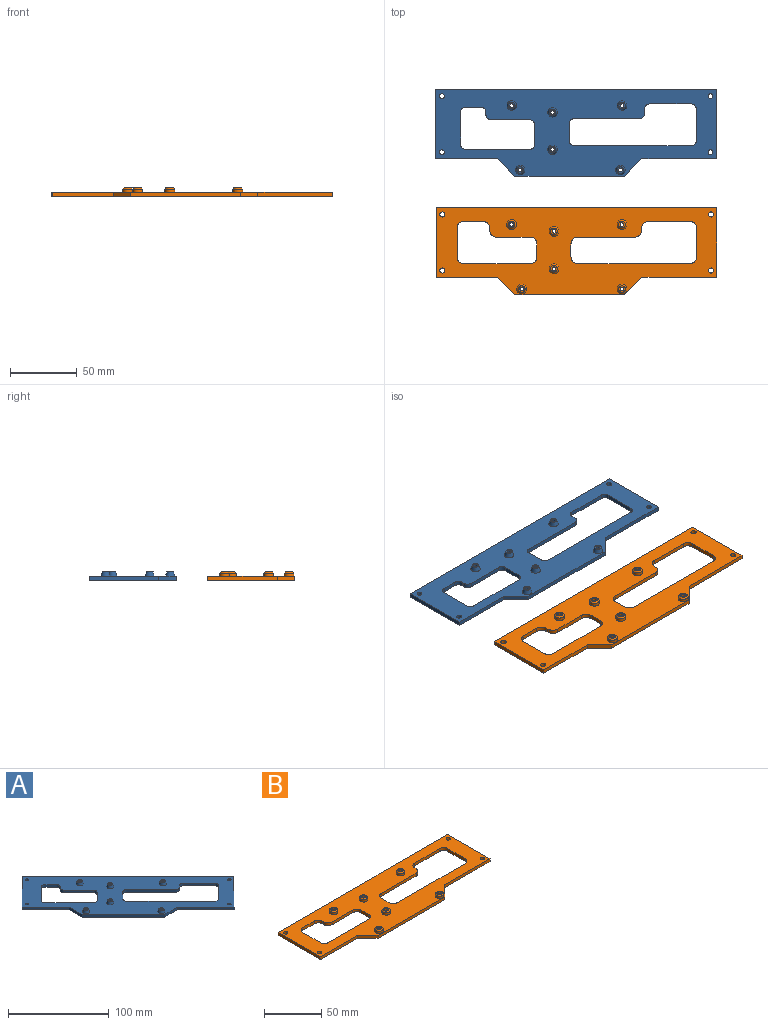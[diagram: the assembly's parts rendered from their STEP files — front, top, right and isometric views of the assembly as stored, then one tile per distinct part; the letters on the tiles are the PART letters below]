
ASSEMBLY  parts=2 mates=2
PART A: 56 faces, bbox 185.7x185.6x6.5 mm
  f0: plane 185.65x185.62mm, normal (0,0,-1), area 8330.5mm2, adj f2,f3,f4,f5,f6,f7,f8,f9
  f1: plane 185.65x185.62mm, normal (0,0,1), area 8139.6mm2, adj f2,f3,f4,f5,f6,f7,f8,f14
  f2: plane 148.96x148.96mm, normal (0.71,0.71,0), area 642.1mm2, adj f0,f1,f3,f18
  f3: plane 36.69x36.69mm, normal (-0.71,0.71,0), area 158.2mm2, adj f0,f1,f2,f4
  f4: plane 33.09x33.09mm, normal (-0.71,-0.71,0), area 142.6mm2, adj f0,f1,f3,f5
  f5: plane 18.17x3.05mm, normal (-1,0,0), area 55.4mm2, adj f0,f1,f4,f6
  f6: plane 58.05x58.05mm, normal (-0.71,-0.71,0), area 250.2mm2, adj f0,f1,f5,f7
  f7: plane 18.24x3.05mm, normal (0,-1,0), area 55.6mm2, adj f0,f1,f6,f8
  f8: plane 39.62x39.62mm, normal (-0.71,-0.71,0), area 170.8mm2, adj f0,f1,f7,f18
  f9: cylinder r=1.4mm len=6.48mm, axis (0,0,1), area 57mm2, adj f0,f21
  f10: cylinder r=1.4mm len=6.48mm, axis (0,0,1), area 57mm2, adj f0,f23
  f11: cylinder r=1.4mm len=6.48mm, axis (0,0,1), area 57mm2, adj f0,f20
  f12: cylinder r=1.4mm len=6.48mm, axis (0,0,1), area 57mm2, adj f0,f24
  f13: cylinder r=1.4mm len=6.48mm, axis (0,0,1), area 57mm2, adj f0,f25
  f14: cylinder r=1.8mm len=3.6mm, axis (0,0,1), area 34.5mm2, adj f0,f1
  f15: cylinder r=1.8mm len=3.6mm, axis (0,0,1), area 34.5mm2, adj f0,f1
  f16: cylinder r=1.8mm len=3.6mm, axis (0,0,1), area 34.5mm2, adj f0,f1
  f17: cylinder r=1.8mm len=3.6mm, axis (0,0,1), area 34.5mm2, adj f0,f1
  f18: plane 36.66x36.66mm, normal (0.71,-0.71,0), area 158mm2, adj f0,f1,f2,f8
  f19: cylinder r=1.4mm len=6.48mm, axis (0,0,1), area 57mm2, adj f0,f22
  f20: plane 4.88x4.88mm, normal (0,0,1), area 12.5mm2, adj f11,f29
  f21: plane 4.91x4.91mm, normal (0,0,1), area 12.8mm2, adj f9,f28
  f22: plane 4.91x4.91mm, normal (0,0,1), area 12.8mm2, adj f19,f26
  f23: plane 4.9x4.9mm, normal (0,0,1), area 12.7mm2, adj f10,f27
  f24: plane 4.89x4.89mm, normal (0,0,1), area 12.6mm2, adj f12,f30
  f25: plane 4.88x4.88mm, normal (0,0,1), area 12.5mm2, adj f13,f31
  f26: cone r=2.46mm half-angle=16.7deg, axis (0,0,-1), area 66.8mm2, adj f1,f22
  f27: cone r=2.45mm half-angle=16.7deg, axis (0,0,-1), area 66.7mm2, adj f1,f23
  f28: cone r=2.45mm half-angle=16.7deg, axis (0,0,-1), area 66.8mm2, adj f1,f21
  f29: cone r=2.44mm half-angle=16.7deg, axis (0,0,-1), area 66.4mm2, adj f1,f20
  f30: cone r=2.44mm half-angle=16.7deg, axis (0,0,-1), area 66.6mm2, adj f1,f24
  f31: cone r=2.44mm half-angle=16.7deg, axis (0,0,-1), area 66.4mm2, adj f1,f25
  f32: plane 61.76x61.76mm, normal (0.71,0.71,0), area 266.2mm2, adj f0,f1,f33,f43
  f33: cylinder r=3.81mm len=5.39mm, axis (0,0,1), area 18.2mm2, adj f0,f1,f32,f34
  f34: plane 16.81x16.81mm, normal (-0.71,0.71,0), area 72.5mm2, adj f0,f1,f33,f35
  f35: cylinder r=3.81mm len=5.39mm, axis (0,0,1), area 18.2mm2, adj f0,f1,f34,f36
  f36: plane 21.92x21.92mm, normal (-0.71,-0.71,0), area 94.5mm2, adj f0,f1,f35,f37
  f37: cylinder r=3.81mm len=5.39mm, axis (0,0,1), area 18.2mm2, adj f0,f1,f36,f38
  f38: plane 3.05x2.38mm, normal (0.71,-0.71,0), area 10.3mm2, adj f0,f1,f37,f39
  f39: cylinder r=3.81mm len=5.39mm, axis (0,0,1), area 18.2mm2, adj f0,f1,f38,f40
  f40: plane 34.45x34.45mm, normal (-0.71,-0.71,0), area 148.5mm2, adj f0,f1,f39,f41
  f41: cylinder r=3.81mm len=5.39mm, axis (0,0,1), area 18.2mm2, adj f0,f1,f40,f42
  f42: plane 9.04x9.04mm, normal (0.71,-0.71,0), area 39mm2, adj f0,f1,f41,f43
  f43: cylinder r=3.81mm len=5.39mm, axis (0,0,1), area 18.2mm2, adj f0,f1,f32,f42
  f44: plane 10.17x10.17mm, normal (-0.71,0.71,0), area 43.8mm2, adj f0,f1,f45,f55
  f45: cylinder r=3.81mm len=5.39mm, axis (0,0,1), area 18.2mm2, adj f0,f1,f44,f46
  f46: plane 20.48x20.48mm, normal (-0.71,-0.71,0), area 88.3mm2, adj f0,f1,f45,f47
  f47: cylinder r=3.81mm len=5.39mm, axis (0,0,1), area 18.2mm2, adj f0,f1,f46,f48
  f48: plane 3.05x1.34mm, normal (-0.71,0.71,0), area 5.8mm2, adj f0,f1,f47,f49
  f49: cylinder r=3.81mm len=5.39mm, axis (0,0,1), area 18.2mm2, adj f0,f1,f48,f50
  f50: plane 8.05x8.05mm, normal (-0.71,-0.71,0), area 34.7mm2, adj f0,f1,f49,f51
  f51: cylinder r=3.81mm len=5.39mm, axis (0,0,1), area 18.2mm2, adj f0,f1,f50,f52
  f52: plane 16.9x16.9mm, normal (0.71,-0.71,0), area 72.8mm2, adj f0,f1,f51,f53
  f53: cylinder r=3.81mm len=5.39mm, axis (0,0,1), area 18.2mm2, adj f0,f1,f52,f54
  f54: plane 33.93x33.93mm, normal (0.71,0.71,0), area 146.2mm2, adj f0,f1,f53,f55
  f55: cylinder r=3.81mm len=5.39mm, axis (0,0,1), area 18.2mm2, adj f0,f1,f44,f54
PART B: 62 faces, bbox 209.6x64.9x6.5 mm
  f0: plane 209.55x64.92mm, normal (0,0,1), area 8053.7mm2, adj f2,f3,f4,f5,f6,f7,f8,f9
  f1: plane 209.55x64.92mm, normal (0,0,-1), area 8263.8mm2, adj f2,f3,f4,f5,f6,f7,f8,f9
  f2: plane 45.69x3mm, normal (0,-1,0), area 137.1mm2, adj f0,f1,f5,f11
  f3: plane 52.07x3mm, normal (1,0,0), area 156.2mm2, adj f0,f1,f4,f9
  f4: plane 209.55x3mm, normal (0,1,0), area 628.6mm2, adj f0,f1,f3,f5
  f5: plane 52.07x3mm, normal (-1,0,0), area 156.2mm2, adj f0,f1,f2,f4
  f6: cylinder r=1.91mm len=3.81mm, axis (0,0,-1), area 35.9mm2, adj f0,f1
  f7: cylinder r=1.91mm len=3.81mm, axis (0,0,-1), area 35.9mm2, adj f0,f1
  f8: cylinder r=1.91mm len=3.81mm, axis (0,0,-1), area 35.9mm2, adj f0,f1
  f9: plane 56.03x3mm, normal (0,-1,0), area 168.1mm2, adj f0,f1,f3,f13
  f10: cylinder r=1.91mm len=3.81mm, axis (0,0,-1), area 35.9mm2, adj f0,f1
  f11: plane 12.87x12.85mm, normal (-0.71,-0.71,0), area 54.6mm2, adj f0,f1,f2,f12
  f12: plane 82.09x3mm, normal (0,-1,0), area 246.3mm2, adj f0,f1,f11,f13
  f13: plane 12.87x12.85mm, normal (0.71,-0.71,0), area 54.6mm2, adj f0,f1,f9,f12
  f14: cylinder r=1.4mm len=6.51mm, axis (0,0,1), area 57.1mm2, adj f1,f31
  f15: cylinder r=1.4mm len=6.51mm, axis (0,0,1), area 57.1mm2, adj f1,f23
  f16: cylinder r=1.4mm len=6.51mm, axis (0,0,1), area 57.1mm2, adj f1,f29
  f17: cylinder r=1.4mm len=6.51mm, axis (0,0,1), area 57.1mm2, adj f1,f21
  f18: cylinder r=1.4mm len=6.51mm, axis (0,0,1), area 57.1mm2, adj f1,f27
  f19: cylinder r=1.4mm len=6.51mm, axis (0,0,1), area 57.1mm2, adj f1,f25
  f20: cylinder r=3.62mm len=7.24mm, axis (0,0,-1), area 53.7mm2, adj f0,f37
  f21: plane 4.95x4.95mm, normal (0,0,1), area 13.1mm2, adj f17,f37
  f22: cylinder r=3.62mm len=7.24mm, axis (0,0,-1), area 53.7mm2, adj f0,f36
  f23: plane 4.95x4.95mm, normal (0,0,1), area 13.1mm2, adj f15,f36
  f24: cylinder r=3.62mm len=7.24mm, axis (0,0,-1), area 53.7mm2, adj f0,f35
  f25: plane 4.95x4.95mm, normal (0,0,1), area 13.1mm2, adj f19,f35
  f26: cylinder r=3.62mm len=7.24mm, axis (0,0,-1), area 53.7mm2, adj f0,f34
  f27: plane 4.95x4.95mm, normal (0,0,1), area 13.1mm2, adj f18,f34
  f28: cylinder r=3.62mm len=7.24mm, axis (0,0,-1), area 53.7mm2, adj f0,f33
  f29: plane 4.95x4.95mm, normal (0,0,1), area 13.1mm2, adj f16,f33
  f30: cylinder r=3.62mm len=7.24mm, axis (0,0,-1), area 53.7mm2, adj f0,f32
  f31: plane 4.95x4.95mm, normal (0,0,1), area 13.1mm2, adj f14,f32
  f32: cone r=2.48mm half-angle=45deg, axis (0,0,-1), area 31mm2, adj f30,f31
  f33: cone r=2.48mm half-angle=45deg, axis (0,0,-1), area 31mm2, adj f28,f29
  f34: cone r=2.48mm half-angle=45deg, axis (0,0,-1), area 31mm2, adj f26,f27
  f35: cone r=2.48mm half-angle=45deg, axis (0,0,-1), area 31mm2, adj f24,f25
  f36: cone r=2.48mm half-angle=45deg, axis (0,0,-1), area 31mm2, adj f22,f23
  f37: cone r=2.48mm half-angle=45deg, axis (0,0,-1), area 31mm2, adj f20,f21
  f38: cylinder r=5.08mm len=5.08mm, axis (0,0,1), area 23.9mm2, adj f0,f1,f39,f49
  f39: plane 9.72x3mm, normal (-1,0,0), area 29.2mm2, adj f0,f1,f38,f40
  f40: cylinder r=5.08mm len=5.08mm, axis (0,0,1), area 23.9mm2, adj f0,f1,f39,f41
  f41: plane 25.28x3mm, normal (0,-1,0), area 75.8mm2, adj f0,f1,f40,f42
  f42: cylinder r=5.08mm len=5.08mm, axis (0,0,1), area 23.9mm2, adj f0,f1,f41,f43
  f43: plane 3x1.71mm, normal (-1,0,0), area 5.1mm2, adj f0,f1,f42,f44
  f44: cylinder r=5.08mm len=5.08mm, axis (0,0,1), area 23.9mm2, adj f0,f1,f43,f45
  f45: plane 14.21x3mm, normal (0,-1,0), area 42.6mm2, adj f0,f1,f44,f46
  f46: cylinder r=5.08mm len=5.08mm, axis (0,0,1), area 23.9mm2, adj f0,f1,f45,f47
  f47: plane 21.59x3mm, normal (1,0,0), area 64.8mm2, adj f0,f1,f46,f48
  f48: cylinder r=5.08mm len=5.08mm, axis (0,0,1), area 23.9mm2, adj f0,f1,f47,f49
  f49: plane 49.65x3mm, normal (0,1,0), area 148.9mm2, adj f0,f1,f38,f48
  f50: plane 9.72x3mm, normal (1,0,0), area 29.2mm2, adj f0,f1,f51,f61
  f51: cylinder r=5.08mm len=5.08mm, axis (0,0,1), area 23.9mm2, adj f0,f1,f50,f52
  f52: plane 83.7x3mm, normal (0,1,0), area 251.1mm2, adj f0,f1,f51,f53
  f53: cylinder r=5.08mm len=5.08mm, axis (0,0,1), area 23.9mm2, adj f0,f1,f52,f54
  f54: plane 21.59x3mm, normal (-1,0,0), area 64.8mm2, adj f0,f1,f53,f55
  f55: cylinder r=5.08mm len=5.08mm, axis (0,0,1), area 23.9mm2, adj f0,f1,f54,f56
  f56: plane 30.78x3mm, normal (0,-1,0), area 92.3mm2, adj f0,f1,f55,f57
  f57: cylinder r=5.08mm len=5.08mm, axis (0,0,1), area 23.9mm2, adj f0,f1,f56,f58
  f58: plane 3x1.71mm, normal (1,0,0), area 5.1mm2, adj f0,f1,f57,f59
  f59: cylinder r=5.08mm len=5.08mm, axis (0,0,1), area 23.9mm2, adj f0,f1,f58,f60
  f60: plane 42.77x3mm, normal (0,-1,0), area 128.3mm2, adj f0,f1,f59,f61
  f61: cylinder r=5.08mm len=5.08mm, axis (0,0,1), area 23.9mm2, adj f0,f1,f50,f60
PLACE A rot(axis=(0,0,1),45deg) t=(-8.71,-57.08,-12.44)mm
PLACE B rot(axis=(0,0,-1),0deg) t=(96.63,-119.54,-15.74)mm
MATE planar B.f3 <-> A.f18  axis (1,0,0) through (96.63,-145.57,-14.24)mm
MATE planar B.f19 <-> A.f10  axis (0,0,-1) through (-25.17,-165.2,-15.74)mm
